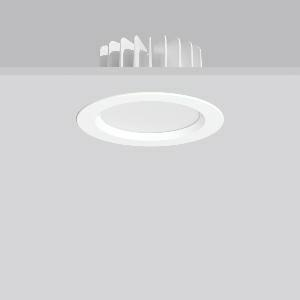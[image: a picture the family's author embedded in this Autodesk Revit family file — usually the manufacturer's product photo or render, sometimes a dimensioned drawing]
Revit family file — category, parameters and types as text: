
# Revit family: ledona_eco_round_901434_002_1_bb01
name_source: partatom
category: Lighting Fixtures
units: mm (PartAtom-declared; Revit-internal decimal feet)

## family parameters
Cut with Voids When Loaded = No
Host = Face
Light Source = No
Part Type = Normal
Room Calculation Point = No
Round Connector Dimension = Use Diameter
Shared = No

## types (1)
- LEDONA ECO round (1 x LED Modul 840, 1600 lm, 4000)
    Apparent Load = 20 VA
    CIE Flux Codes = 49 81 97 100 100
    Color Rendering = 80
    Color Temperature = 4000
    Default Elevation = 1800 mm
    Height = 0 mm  [stored 0 ft]
    Lamp = 1 x LED Modul 840
    Lamp Light Flux = 1600 lm
    Lamp count = 1
    Length = 180 mm  [stored 0.590551 ft]
    Lifetime = 50000 h
    Luminous efficacy = 80 lm/W
    Manufacturer = RZB
    ModVariant = No
    Model = 901434.002.1
    Mounting Place = Ceiling
    Mounting Type = Recessed
    Number of Poles = 1
    OnlyDefault = Yes
    Power Factor = 1
    Product Name = LEDONA ECO round
    Product group = Recessed downlights
    ProductGroupID = 402
    Protection Class = Protection class I
    Protection Degree = IP 65
    RLX_Detail_Level = 1
    RLX_Emergency_Light_Flux = 0 lm
    RLX_Emergency_Type = 0
    RLX_Emergency_Type_DB = No
    RlxData = <blob elided: 35821 chars, md5=b07954ef>
    Socket = socket
    Standby Power = 0 W
    System Light Flux = 1600 lm
    System Power = 20 W
    Type Comments = ALEA SPOT
    Type Image = 901434.002.jpg
    URL = http://relux.com
    VarID = ---
    Voltage = 230 V
    Voltage Range = 220-240 V
    Weight = 0.00 kg
    Width = 0 mm  [stored 0 ft]

note: [stored X ft] marks values corroborated as IEEE doubles in the binary element streams (Revit-internal decimal feet)

## geometry (parser evidence)
native form markers: Blend x4, Sweep x10
no freeform markers — native parametric forms only
